# Revit family: FP_Revit20_CG762DNGGB4_Cooktop_90001821A
name_source: partatom
category: Specialty Equipment
units: mm (PartAtom-declared; Revit-internal decimal feet)

## family parameters
Always vertical = Yes
Cut with Voids When Loaded = Yes
OmniClass Number = 23.40.40.14.17.11
OmniClass Title = Cookers, Ovens, Stoves
Part Type = Normal
Room Calculation Point = No
Round Connector Dimension = Use Diameter
Shared = No
Work Plane-Based = No

## types (1)
- JZT-CG762DNGGB4
    Cavity - Depth = 410 mm  [stored 1.34514 ft]
    Cavity - Height = 59 mm
    Cavity - Width = 715 mm  [stored 2.3458 ft]
    Chassis - Depth = 405 mm
    Chassis - Height = 59 mm
    Chassis - Width = 706 mm  [stored 2.31627 ft]
    Clearance - Below Combustible = 70 mm  [stored 0.229659 ft]
    Clearance - Below Non-Combustible = 65 mm  [stored 0.213255 ft]
    Clearance - Overhead Combustible = 650 mm  [stored 2.13255 ft]
    Clearance - Overhead Non-Combustible = 500 mm  [stored 1.64042 ft]
    Clearance - Overhead Rangehood = 650 mm  [stored 2.13255 ft]
    Clearance - Rear Combustible = 125 mm  [stored 0.410105 ft]
    Clearance - Rear Non-Combustible = 45 mm  [stored 0.147638 ft]
    Clearance - Side Combustible = 115 mm  [stored 0.377297 ft]
    Connector Note - Electrical = 230 V, 10 A, fused electrical supply
    Connector Note - Gas = NG 1 kPa (4" WC) Connection is Rp 1/2" (ISO7-1)
    Default Elevation = 0 mm  [stored 0 ft]
    Description = 76cm Series 9 2 Burner Gas Cooktop, Natural Gas
    Manufacturer = Fisher & Paykel Appliances
    Material - Body = Fisher & Paykel - Grey
    Material - Burners & Trivets = Fisher & Paykel - Black, Matte
    Material - Cooktop = Fisher & Paykel - Glass, Black
    Material - Trim = Fisher & Paykel - Aluminium, Dark
    Model = JZT-CG762DNGGB4
    Product - Depth = 450 mm  [stored 1.47638 ft]
    Product - Height = 59 mm
    Product - Width = 759 mm  [stored 2.49016 ft]
    URL = www.fisherpaykel.com
    Visibility - Clearance Required = Yes

note: [stored X ft] marks values corroborated as IEEE doubles in the binary element streams (Revit-internal decimal feet)

## geometry (parser evidence)
native form markers: Sweep x12
no freeform markers — native parametric forms only
